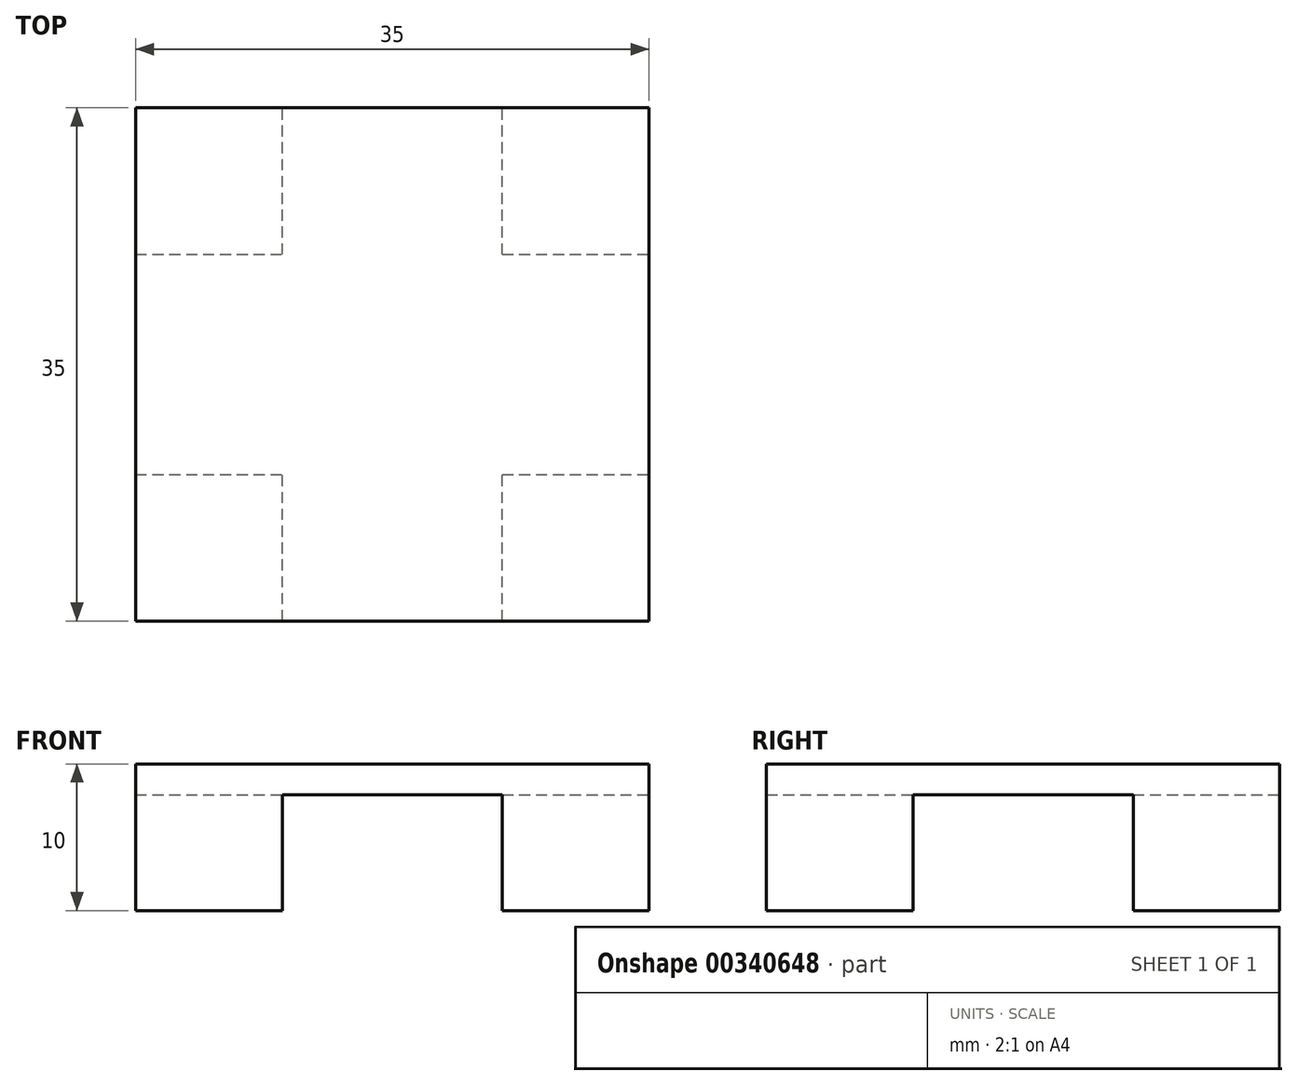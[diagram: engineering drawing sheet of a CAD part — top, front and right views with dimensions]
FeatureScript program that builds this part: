
annotation { "Feature Type Name" : "Feature", "Feature Type Description" : "" }
export const myFeature = defineFeature(function(context is Context, id is Id, definition is map)
    precondition{}
    {
        {
            var Q0;
            Q0=qCreatedBy(makeId("Top.planeOp"),FACE);
            var sketch = newSketch(context, id + "F0", { "sketchPlane" : qUnion([Q0])});
            skLineSegment(sketch, "E0.bottom", {"start": v(5, 5) * mm, "end": v(15, 5) * mm});
            skLineSegment(sketch, "E0.top", {"start": v(5, 15) * mm, "end": v(15, 15) * mm});
            skLineSegment(sketch, "E0.left", {"start": v(5, 5) * mm, "end": v(5, 15) * mm});
            skLineSegment(sketch, "E0.right", {"start": v(15, 5) * mm, "end": v(15, 15) * mm});
            skLineSegment(sketch, "E1.0.1.0", {"start": v(5, 40) * mm, "end": v(15, 40) * mm});
            skLineSegment(sketch, "E1.0.1.1", {"start": v(15, 30) * mm, "end": v(15, 40) * mm});
            skLineSegment(sketch, "E1.0.1.2", {"start": v(5, 30) * mm, "end": v(15, 30) * mm});
            skLineSegment(sketch, "E1.0.1.3", {"start": v(5, 30) * mm, "end": v(5, 40) * mm});
            skLineSegment(sketch, "E1.1.0.0", {"start": v(30, 15) * mm, "end": v(40, 15) * mm});
            skLineSegment(sketch, "E1.1.0.1", {"start": v(40, 5) * mm, "end": v(40, 15) * mm});
            skLineSegment(sketch, "E1.1.0.2", {"start": v(30, 5) * mm, "end": v(40, 5) * mm});
            skLineSegment(sketch, "E1.1.0.3", {"start": v(30, 5) * mm, "end": v(30, 15) * mm});
            skLineSegment(sketch, "E1.1.1.0", {"start": v(30, 40) * mm, "end": v(40, 40) * mm});
            skLineSegment(sketch, "E1.1.1.1", {"start": v(40, 30) * mm, "end": v(40, 40) * mm});
            skLineSegment(sketch, "E1.1.1.2", {"start": v(30, 30) * mm, "end": v(40, 30) * mm});
            skLineSegment(sketch, "E1.1.1.3", {"start": v(30, 30) * mm, "end": v(30, 40) * mm});
            skLineSegment(sketch, "E1.direction1", {"start": v(5, 15) * mm, "end": v(30, 15) * mm, "construction": true});
            skLineSegment(sketch, "E1.direction2", {"start": v(5, 15) * mm, "end": v(5, 40) * mm, "construction": true});
            skSolve(sketch);
        }
        {
            var Q0;
            Q0=makeQuery(id+"F0.imprint","IMPRINT",FACE,{"disambiguationData":[TD([[makeQuery(id+"F0.imprint","IMPRINT",EDGE,{"derivedFrom":sQuery(id+"F0.wireOp",EDGE,"E0.bottom")}),1.0]])]});
            var Q1;
            Q1=makeQuery(id+"F0.imprint","IMPRINT",FACE,{"disambiguationData":[TD([[makeQuery(id+"F0.imprint","IMPRINT",EDGE,{"derivedFrom":sQuery(id+"F0.wireOp",EDGE,"E1.0.1.0")}),-1.0]])]});
            var Q2;
            Q2=makeQuery(id+"F0.imprint","IMPRINT",FACE,{"disambiguationData":[TD([[makeQuery(id+"F0.imprint","IMPRINT",EDGE,{"derivedFrom":sQuery(id+"F0.wireOp",EDGE,"E1.1.1.0")}),-1.0]])]});
            var Q3;
            Q3=makeQuery(id+"F0.imprint","IMPRINT",FACE,{"disambiguationData":[TD([[makeQuery(id+"F0.imprint","IMPRINT",EDGE,{"derivedFrom":sQuery(id+"F0.wireOp",EDGE,"E1.1.0.0")}),-1.0]])]});
            extrude(context, id + "F1", {"entities" : qUnion([Q0, Q1, Q2, Q3]), "depth" : 10 * mm});
        }
        {
            var Q0;
            Q0=makeQuery(id+"F1.opExtrude","CAP_FACE",FACE,{"disambiguationData":[OSD([sQuery(id+"F0.wireOp",EDGE,"E0.bottom"),sQuery(id+"F0.wireOp",EDGE,"E0.top"),sQuery(id+"F0.wireOp",EDGE,"E0.left"),sQuery(id+"F0.wireOp",EDGE,"E0.right")])],"isStart":false});
            var sketch = newSketch(context, id + "F2", { "sketchPlane" : qUnion([Q0])});
            skLineSegment(sketch, "E2.bottom", {"start": v(5, 5) * mm, "end": v(40, 5) * mm});
            skLineSegment(sketch, "E2.top", {"start": v(5, 40) * mm, "end": v(40, 40) * mm});
            skLineSegment(sketch, "E2.left", {"start": v(5, 5) * mm, "end": v(5, 40) * mm});
            skLineSegment(sketch, "E2.right", {"start": v(40, 5) * mm, "end": v(40, 40) * mm});
            skSolve(sketch);
        }
        {
            var Q0;
            Q0 = qSketchRegion(id + "F2", true);
            extrude(context, id + "F3", {"entities" : qUnion([Q0]), "operationType" : NewBodyOperationType.ADD, "oppositeDirection" : true, "depth" : 2.1 * mm});
        }
    });
